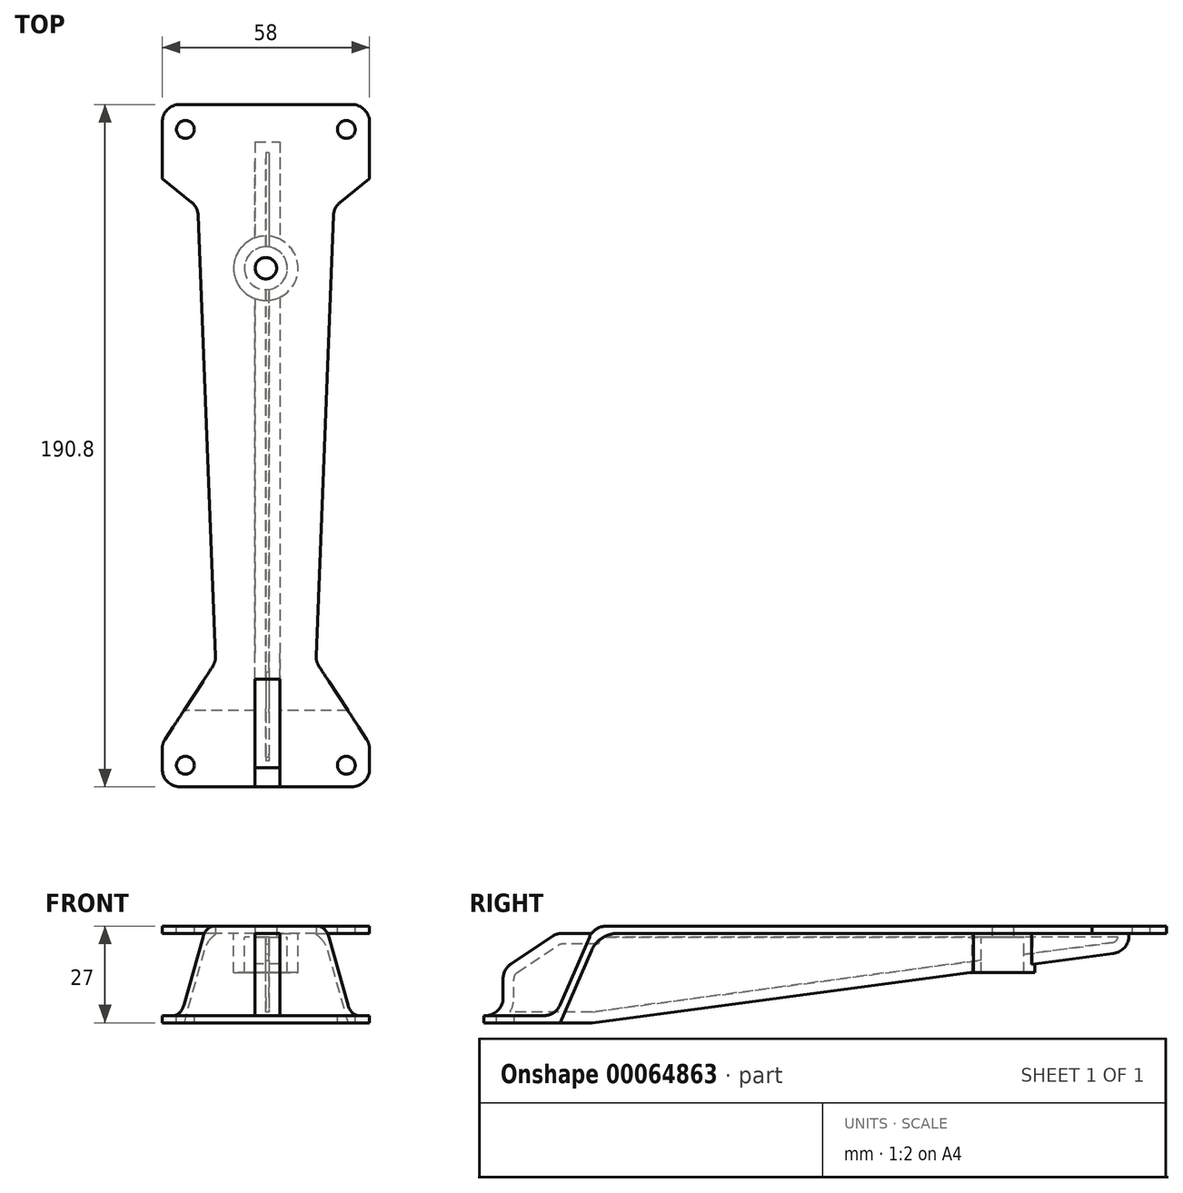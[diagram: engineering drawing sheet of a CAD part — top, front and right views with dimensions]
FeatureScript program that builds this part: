
annotation { "Feature Type Name" : "Feature", "Feature Type Description" : "" }
export const myFeature = defineFeature(function(context is Context, id is Id, definition is map)
    precondition{}
    {
        {
            var Q0;
            Q0=qCreatedBy(makeId("Right.planeOp"),FACE);
            var sketch = newSketch(context, id + "F0", { "sketchPlane" : qUnion([Q0])});
            skLineSegment(sketch, "E0.bottom", {"start": v(-67.89, -2) * mm, "end": v(90.8, -2) * mm});
            skLineSegment(sketch, "E0.top", {"start": v(-69.2, 0) * mm, "end": v(90.8, 0) * mm});
            skLineSegment(sketch, "E0.right", {"start": v(90.8, -2) * mm, "end": v(90.8, 0) * mm});
            skLineSegment(sketch, "E1.bottom", {"start": v(-100, -25) * mm, "end": v(-80, -25) * mm});
            skLineSegment(sketch, "E1.top", {"start": v(-100, -27) * mm, "end": v(-78.69, -27) * mm});
            skLineSegment(sketch, "E1.left", {"start": v(-100, -25) * mm, "end": v(-100, -27) * mm});
            skLineSegment(sketch, "E2", {"start": v(-69.2, 0) * mm, "end": v(-80, -25) * mm});
            skLineSegment(sketch, "E3.0", {"start": v(-67.89, -2) * mm, "end": v(-78.69, -27) * mm});
            skSolve(sketch);
        }
        {
            var Q0;
            Q0=makeQuery(id+"F0.imprint","IMPRINT",FACE,{"disambiguationData":[TD([[makeQuery(id+"F0.imprint","IMPRINT",EDGE,{"derivedFrom":sQuery(id+"F0.wireOp",EDGE,"E0.bottom")}),1.0]])]});
            extrude(context, id + "F1", {"entities" : qUnion([Q0]), "depth" : (45 + 3 + 10) / 2 * mm, "hasSecondDirection" : true, "secondDirectionOppositeDirection" : true, "secondDirectionDepth" : 29 * mm});
        }
        {
            var Q0;
            Q0=makeQuery(id+"F1.opExtrude","SWEPT_FACE",FACE,{"disambiguationData":[OSD([sQuery(id+"F0.wireOp",EDGE,"E0.top")])]});
            var sketch = newSketch(context, id + "F2", { "sketchPlane" : qUnion([Q0])});
            skCircle(sketch, "E4", {"center": v(22.5, 83.8) * mm, "radius": 2.5 * mm});
            skCircle(sketch, "E5", {"center": v(-22.5, 83.8) * mm, "radius": 2.5 * mm});
            skCircle(sketch, "E6", {"center": v(-22.5, -94) * mm, "radius": 2.5 * mm});
            skCircle(sketch, "E7", {"center": v(22.5, -94) * mm, "radius": 2.5 * mm});
            skLineSegment(sketch, "E8", {"start": v(29, -88) * mm, "end": v(14, -65) * mm});
            skLineSegment(sketch, "E9", {"start": v(14, -65) * mm, "end": v(19, 62) * mm});
            skLineSegment(sketch, "E10", {"start": v(19, 62) * mm, "end": v(29, 70) * mm});
            skLineSegment(sketch, "E11", {"start": v(29, 70) * mm, "end": v(29, -88) * mm});
            skLineSegment(sketch, "E12", {"start": v(29, -88) * mm, "end": v(29, 70) * mm});
            skLineSegment(sketch, "E13", {"start": v(0, -88.5) * mm, "end": v(0, 58.33) * mm, "construction": true});
            skLineSegment(sketch, "E14.MirrorCS", {"start": v(-29, -88) * mm, "end": v(-14, -65) * mm});
            skLineSegment(sketch, "E15.MirrorCS", {"start": v(-14, -65) * mm, "end": v(-19, 62) * mm});
            skLineSegment(sketch, "E16.MirrorCS", {"start": v(-19, 62) * mm, "end": v(-29, 70) * mm});
            skLineSegment(sketch, "E17.MirrorCS", {"start": v(-29, -88) * mm, "end": v(-29, 70) * mm});
            skSolve(sketch);
        }
        {
            var Q0;
            Q0=makeQuery(id+"F2.imprint","IMPRINT",FACE,{"disambiguationData":[TD([[makeQuery(id+"F2.imprint","IMPRINT",EDGE,{"derivedFrom":sQuery(id+"F2.wireOp",EDGE,"E7")}),1.0]])]});
            var Q1;
            Q1=makeQuery(id+"F2.imprint","IMPRINT",FACE,{"disambiguationData":[TD([[makeQuery(id+"F2.imprint","IMPRINT",EDGE,{"derivedFrom":sQuery(id+"F2.wireOp",EDGE,"E6")}),1.0]])]});
            var Q2;
            Q2=makeQuery(id+"F2.imprint","IMPRINT",FACE,{"disambiguationData":[TD([[makeQuery(id+"F2.imprint","IMPRINT",EDGE,{"derivedFrom":sQuery(id+"F2.wireOp",EDGE,"E4")}),1.0]])]});
            var Q3;
            Q3=makeQuery(id+"F2.imprint","IMPRINT",FACE,{"disambiguationData":[TD([[makeQuery(id+"F2.imprint","IMPRINT",EDGE,{"derivedFrom":sQuery(id+"F2.wireOp",EDGE,"E5")}),1.0]])]});
            extrude(context, id + "F3", {"entities" : qUnion([Q0, Q1, Q2, Q3]), "operationType" : NewBodyOperationType.REMOVE, "oppositeDirection" : true, "depth" : 100 * mm});
        }
        {
            var Q0;
            {var subQ5=sQuery(id+"F2.wireOp",EDGE,"E9");Q0=makeQuery(id+"F2.imprint","IMPRINT",FACE,{"disambiguationData":[TD([[makeQuery(id+"F2.imprint","IMPRINT",EDGE,{"derivedFrom":subQ5}),-1.0]])]});}
            var Q1;
            {var subQ0=sQuery(id+"F2.wireOp",EDGE,"E12");var subQ1=sQuery(id+"F2.wireOp",EDGE,"E8");var subQ2=makeQuery(id+"F2.imprint","INTERSECT",VERTEX,{"derivedFrom":[subQ1,subQ0]});Q1=makeQuery(id+"F2.imprint","IMPRINT",FACE,{"disambiguationData":[TD([[makeQuery(id+"F2.imprint","IMPRINT",EDGE,{"disambiguationData":[TD([[subQ2,-1.0]])],"derivedFrom":subQ1}),-1.0]])]});}
            var Q2;
            {var subQ0=sQuery(id+"F2.wireOp",EDGE,"E17.MirrorCS");var subQ1=sQuery(id+"F2.wireOp",EDGE,"E14.MirrorCS");var subQ2=makeQuery(id+"F2.imprint","INTERSECT",VERTEX,{"derivedFrom":[subQ1,subQ0]});Q2=makeQuery(id+"F2.imprint","IMPRINT",FACE,{"disambiguationData":[TD([[makeQuery(id+"F2.imprint","IMPRINT",EDGE,{"disambiguationData":[TD([[subQ2,-1.0]])],"derivedFrom":subQ1}),1.0]])]});}
            var Q3;
            {var subQ5=sQuery(id+"F2.wireOp",EDGE,"E15.MirrorCS");Q3=makeQuery(id+"F2.imprint","IMPRINT",FACE,{"disambiguationData":[TD([[makeQuery(id+"F2.imprint","IMPRINT",EDGE,{"derivedFrom":subQ5}),1.0]])]});}
            extrude(context, id + "F4", {"entities" : qUnion([Q0, Q1, Q2, Q3]), "operationType" : NewBodyOperationType.REMOVE, "oppositeDirection" : true, "depth" : 30 * mm});
        }
        {
            var Q0;
            Q0=makeQuery(id+"F1.opExtrude","CAP_EDGE",EDGE,{"disambiguationData":[OSD([sQuery(id+"F0.wireOp",EDGE,"E1.left")])],"isStart":true});
            var Q1;
            Q1=makeQuery(id+"F4.boolean.opBoolean","COPY",EDGE,{"derivedFrom":makeQuery(id+"F4.opExtrude","SWEPT_EDGE",EDGE,{"disambiguationData":[OSD([sQuery(id+"F2.wireOp",EDGE,"E14.MirrorCS"),sQuery(id+"F2.wireOp",EDGE,"E17.MirrorCS")])]})});
            var Q2;
            Q2=makeQuery(id+"F1.opExtrude","CAP_EDGE",EDGE,{"disambiguationData":[OSD([sQuery(id+"F0.wireOp",EDGE,"E1.left")])],"isStart":false});
            var Q3;
            Q3=makeQuery(id+"F4.boolean.opBoolean","COPY",EDGE,{"derivedFrom":makeQuery(id+"F4.opExtrude","SWEPT_EDGE",EDGE,{"disambiguationData":[OSD([sQuery(id+"F2.wireOp",EDGE,"E8"),sQuery(id+"F2.wireOp",EDGE,"E12")])]})});
            var Q4;
            Q4=makeQuery(id+"F4.boolean.opBoolean","COPY",EDGE,{"derivedFrom":makeQuery(id+"F4.opExtrude","SWEPT_EDGE",EDGE,{"disambiguationData":[OSD([sQuery(id+"F2.wireOp",EDGE,"E8"),sQuery(id+"F2.wireOp",EDGE,"E9")])]})});
            var Q5;
            Q5=makeQuery(id+"F4.boolean.opBoolean","COPY",EDGE,{"derivedFrom":makeQuery(id+"F4.opExtrude","SWEPT_EDGE",EDGE,{"disambiguationData":[OSD([sQuery(id+"F2.wireOp",EDGE,"E14.MirrorCS"),sQuery(id+"F2.wireOp",EDGE,"E15.MirrorCS")])]})});
            var Q6;
            Q6=makeQuery(id+"F1.opExtrude","SWEPT_EDGE",EDGE,{"disambiguationData":[OSD([sQuery(id+"F0.wireOp",EDGE,"E1.bottom"),sQuery(id+"F0.wireOp",EDGE,"E2")])]});
            var Q7;
            Q7=makeQuery(id+"F1.opExtrude","CAP_EDGE",EDGE,{"disambiguationData":[OSD([sQuery(id+"F0.wireOp",EDGE,"E0.right")])],"isStart":true});
            var Q8;
            Q8=makeQuery(id+"F4.boolean.opBoolean","COPY",EDGE,{"derivedFrom":makeQuery(id+"F4.opExtrude","SWEPT_EDGE",EDGE,{"disambiguationData":[OSD([sQuery(id+"F0.wireOp",EDGE,"E0.top"),sQuery(id+"F2.wireOp",EDGE,"E16.MirrorCS"),sQuery(id+"F2.wireOp",EDGE,"E17.MirrorCS")])]})});
            var Q9;
            Q9=makeQuery(id+"F1.opExtrude","CAP_EDGE",EDGE,{"disambiguationData":[OSD([sQuery(id+"F0.wireOp",EDGE,"E0.right")])],"isStart":false});
            var Q10;
            Q10=makeQuery(id+"F4.boolean.opBoolean","COPY",EDGE,{"derivedFrom":makeQuery(id+"F4.opExtrude","SWEPT_EDGE",EDGE,{"disambiguationData":[OSD([sQuery(id+"F0.wireOp",EDGE,"E0.top"),sQuery(id+"F2.wireOp",EDGE,"E10"),sQuery(id+"F2.wireOp",EDGE,"E12")])]})});
            var Q11;
            Q11=makeQuery(id+"F4.boolean.opBoolean","COPY",EDGE,{"derivedFrom":makeQuery(id+"F4.opExtrude","SWEPT_EDGE",EDGE,{"disambiguationData":[OSD([sQuery(id+"F2.wireOp",EDGE,"E9"),sQuery(id+"F2.wireOp",EDGE,"E10")])]})});
            var Q12;
            Q12=makeQuery(id+"F4.boolean.opBoolean","COPY",EDGE,{"derivedFrom":makeQuery(id+"F4.opExtrude","SWEPT_EDGE",EDGE,{"disambiguationData":[OSD([sQuery(id+"F2.wireOp",EDGE,"E15.MirrorCS"),sQuery(id+"F2.wireOp",EDGE,"E16.MirrorCS")])]})});
            fillet(context, id + "F5", {"entities" : qUnion([Q0, Q1, Q2, Q3, Q4, Q5, Q6, Q7, Q8, Q9, Q10, Q11, Q12]), "radius" : 5 * mm, "tangentPropagation" : true, "allowEdgeOverflow" : false});
        }
        {
            var Q0;
            Q0=makeQuery(id+"F1.opExtrude","SWEPT_EDGE",EDGE,{"disambiguationData":[OSD([sQuery(id+"F0.wireOp",EDGE,"E0.top"),sQuery(id+"F0.wireOp",EDGE,"E2")])]});
            fillet(context, id + "F6", {"entities" : qUnion([Q0]), "radius" : 5 * mm, "tangentPropagation" : true, "allowEdgeOverflow" : false});
        }
        {
            var Q0;
            Q0=makeQuery(id+"F1.opExtrude","SWEPT_EDGE",EDGE,{"disambiguationData":[OSD([sQuery(id+"F0.wireOp",EDGE,"E0.bottom"),sQuery(id+"F0.wireOp",EDGE,"E3.0")])]});
            fillet(context, id + "F7", {"entities" : qUnion([Q0]), "radius" : 8 * mm, "tangentPropagation" : true, "allowEdgeOverflow" : false});
        }
        {
            var Q0;
            Q0=makeQuery(id+"F1.opExtrude","SWEPT_FACE",FACE,{"disambiguationData":[OSD([sQuery(id+"F0.wireOp",EDGE,"E0.bottom")])]});
            var sketch = newSketch(context, id + "F8", { "sketchPlane" : qUnion([Q0])});
            skLineSegment(sketch, "E18.left", {"start": v(-3, -55.33) * mm, "end": v(-3, -81.52) * mm});
            skLineSegment(sketch, "E19.bottom", {"start": v(-3, -80.33) * mm, "end": v(3, -80.33) * mm});
            skLineSegment(sketch, "E19.left", {"start": v(-3, -80.33) * mm, "end": v(-3, 88.3) * mm});
            skLineSegment(sketch, "E20.bottom", {"start": v(-3, -80.33) * mm, "end": v(3.93, -80.33) * mm});
            skLineSegment(sketch, "E20.top", {"start": v(-3, 94.67) * mm, "end": v(3.93, 94.67) * mm});
            skLineSegment(sketch, "E20.left", {"start": v(-3, -80.33) * mm, "end": v(-3, 94.67) * mm});
            skLineSegment(sketch, "E20.right", {"start": v(3.93, -80.33) * mm, "end": v(3.93, 94.67) * mm});
            skSolve(sketch);
        }
        {
            var Q0;
            {var subQ0=sQuery(id+"F8.wireOp",EDGE,"E20.top");Q0=makeQuery(id+"F8.imprint","IMPRINT",FACE,{"disambiguationData":[TD([[makeQuery(id+"F8.imprint","IMPRINT",EDGE,{"derivedFrom":subQ0}),-1.0]])]});}
            var Q1;
            {var subQ5=sQuery(id+"F8.wireOp",EDGE,"E20.bottom");var subQ9=makeQuery(id+"F8.imprint","IMPRINT",VERTEX,{"derivedFrom":subQ5});Q1=makeQuery(id+"F8.imprint","IMPRINT",FACE,{"disambiguationData":[TD([[makeQuery(id+"F8.imprint","IMPRINT",EDGE,{"disambiguationData":[TD([[subQ9,1.0]])],"derivedFrom":subQ5}),1.0]])]});}
            extrude(context, id + "F9", {"entities" : qUnion([Q0, Q1]), "operationType" : NewBodyOperationType.ADD, "depth" : 25 * mm});
        }
        {
            var Q0;
            Q0=makeQuery(id+"F9.opExtrude","CAP_EDGE",EDGE,{"disambiguationData":[OSD([sQuery(id+"F8.wireOp",EDGE,"E20.top")])],"isStart":true});
            chamfer(context, id + "F10", {"entities" : qUnion([Q0]), "chamferType" : ChamferType.TWO_OFFSETS, "width1" : 15 * mm, "oppositeDirection" : false, "width2" : 10 * mm, "tangentPropagation" : true});
        }
        {
            var Q0;
            {var subQ0=sQuery(id+"F8.wireOp",EDGE,"E20.top");Q0=makeQuery(id+"F10.opChamfer","BLEND_EDGE",EDGE,{"blendedFrom":[makeQuery(id+"F9.opExtrude","CAP_EDGE",EDGE,{"disambiguationData":[OSD([subQ0])],"isStart":true}),makeQuery(id+"F9.opExtrude","SWEPT_FACE",FACE,{"disambiguationData":[OSD([subQ0])]})],"blendedInto":[makeQuery(id+"F9.opExtrude","SWEPT_FACE",FACE,{"disambiguationData":[OSD([subQ0])]})]});}
            var Q1;
            {var subQ0=sQuery(id+"F8.wireOp",EDGE,"E20.top");Q1=makeQuery(id+"F10.opChamfer","BLEND_EDGE",EDGE,{"blendedFrom":[makeQuery(id+"F9.opExtrude","CAP_EDGE",EDGE,{"disambiguationData":[OSD([subQ0])],"isStart":true}),makeQuery(id+"F9.opExtrude","CAP_FACE",FACE,{"disambiguationData":[OSD([sQuery(id+"F8.wireOp",EDGE,"E20.bottom"),sQuery(id+"F8.wireOp",EDGE,"E20.left"),sQuery(id+"F8.wireOp",EDGE,"E20.right"),subQ0])],"isStart":true})],"blendedInto":[makeQuery(id+"F9.opExtrude","CAP_FACE",FACE,{"disambiguationData":[OSD([sQuery(id+"F8.wireOp",EDGE,"E20.bottom"),sQuery(id+"F8.wireOp",EDGE,"E20.left"),sQuery(id+"F8.wireOp",EDGE,"E20.right"),subQ0])],"isStart":true})]});}
            var Q2;
            Q2=makeQuery(id+"F9.boolean.opBoolean","INTERSECT",EDGE,{"derivedFrom":[makeQuery(id+"F1.opExtrude","SWEPT_FACE",FACE,{"disambiguationData":[OSD([sQuery(id+"F0.wireOp",EDGE,"E1.bottom")])]}),makeQuery(id+"F9.opExtrude","SWEPT_FACE",FACE,{"disambiguationData":[OSD([sQuery(id+"F8.wireOp",EDGE,"E20.top")])]})]});
            fillet(context, id + "F11", {"entities" : qUnion([Q0, Q1, Q2]), "radius" : 5 * mm, "tangentPropagation" : true, "allowEdgeOverflow" : false});
        }
        {
            var Q0;
            Q0=makeQuery(id+"F9.opExtrude","CAP_EDGE",EDGE,{"disambiguationData":[OSD([sQuery(id+"F8.wireOp",EDGE,"E20.bottom")])],"isStart":false});
            chamfer(context, id + "F12", {"entities" : qUnion([Q0]), "chamferType" : ChamferType.TWO_OFFSETS, "width1" : 150 * mm, "oppositeDirection" : false, "width2" : 20 * mm, "tangentPropagation" : true});
        }
        {
            var Q0;
            {var subQ0=sQuery(id+"F8.wireOp",EDGE,"E20.bottom");Q0=makeQuery(id+"F12.opChamfer","BLEND_EDGE",EDGE,{"blendedFrom":[makeQuery(id+"F9.opExtrude","CAP_EDGE",EDGE,{"disambiguationData":[OSD([subQ0])],"isStart":false}),makeQuery(id+"F9.opExtrude","SWEPT_FACE",FACE,{"disambiguationData":[OSD([subQ0])]})],"blendedInto":[makeQuery(id+"F9.opExtrude","SWEPT_FACE",FACE,{"disambiguationData":[OSD([subQ0])]})]});}
            fillet(context, id + "F13", {"entities" : qUnion([Q0]), "radius" : 5 * mm, "tangentPropagation" : true, "allowEdgeOverflow" : false});
        }
        {
            var Q0;
            Q0=makeQuery(id+"F1.opExtrude","SWEPT_FACE",FACE,{"disambiguationData":[OSD([sQuery(id+"F0.wireOp",EDGE,"E0.bottom")])]});
            var sketch = newSketch(context, id + "F14", { "sketchPlane" : qUnion([Q0])});
            skCircle(sketch, "E21", {"center": v(0, -45) * mm, "radius": 9 * mm});
            skSolve(sketch);
        }
        {
            var Q0;
            Q0 = qSketchRegion(id + "F14", true);
            extrude(context, id + "F15", {"entities" : qUnion([Q0]), "operationType" : NewBodyOperationType.ADD, "depth" : 11 * mm});
        }
        {
            var Q0;
            Q0=makeQuery(id+"F15.opExtrude","CAP_FACE",FACE,{"disambiguationData":[OSD([sQuery(id+"F14.wireOp",EDGE,"E21")])],"isStart":false});
            shell(context, id + "F16", {"entities" : qUnion([Q0]), "thickness" : 3 * mm});
        }
        {
            var Q0;
            Q0=makeQuery(id+"F16.opShell","OFFSET_FACE",FACE,{"disambiguationData":[OSD([sQuery(id+"F0.wireOp",EDGE,"E0.top")])]});
            var sketch = newSketch(context, id + "F17", { "sketchPlane" : qUnion([Q0])});
            skCircle(sketch, "E22", {"center": v(0, -45) * mm, "radius": 3 * mm});
            skSolve(sketch);
        }
        {
            var Q0;
            Q0=makeQuery(id+"F17.imprint","IMPRINT",FACE,{"disambiguationData":[TD([[makeQuery(id+"F17.imprint","IMPRINT",EDGE,{"derivedFrom":sQuery(id+"F17.wireOp",EDGE,"E22")}),1.0]])]});
            extrude(context, id + "F18", {"entities" : qUnion([Q0]), "operationType" : NewBodyOperationType.REMOVE, "oppositeDirection" : true, "depth" : 25 * mm});
        }
    });
